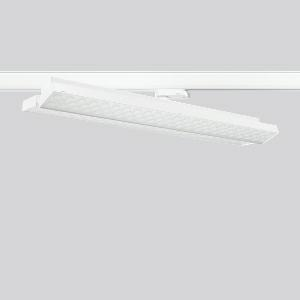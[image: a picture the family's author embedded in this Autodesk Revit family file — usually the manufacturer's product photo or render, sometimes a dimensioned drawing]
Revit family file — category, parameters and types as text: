
# Revit family: tx-move_742163_002_3_76_4216
name_source: partatom
category: Lighting Fixtures
units: mm (PartAtom-declared; Revit-internal decimal feet)

## family parameters
Cut with Voids When Loaded = No
Host = Face
Light Source = No
Part Type = Normal
Room Calculation Point = No
Round Connector Dimension = Use Diameter
Shared = No

## types (1)
- MultiLumen 1 (1 x LED Modul 835, 2875 lm, 3500)
    Apparent Load = 41 VA
    CIE Flux Codes = 65 90 98 100 100
    Color Rendering = 80
    Color Temperature = 3500
    Default Elevation = 1800 mm
    Description = Series: TX-MOVE
Multifunctional surface-mounted spotlight for area lighting. Very flat design. Housing: sheet steel, powder-coated. Rotation range: 356°. Swivel range: 90°. Consistent alignment possible with visible tilt scale. High-efficiency LED units with optimum light control thanks to clear plastic (PC) lens optics. Spezielle Mikrostrukturen reduzieren Gelbsaum. Asymmetrical light distribution. With adapter for RZB 3-circuit DALI tracks. Suitable for Track on ceiling. MultiLumen: Luminous flux adjustable in 3 steps. Factory setting is the highest luminous flux. Environmentally friendly and resource-saving due to replaceable and recyclable components. 
Colour: traffic white, matt (RAL 9016)
Length: 570 mm
Width: 119 mm
Height: 88 mm
Lamp: LED
Socket: without socket
Colour temperature: 3500K
Colour rendering index (CRI): 80
System power: 41 W
Rated luminous flux: 5750 lm
Luminous efficiency: 140 lm/W
System power 2: 57 W
Rated luminous flux 2: 7750 lm
Luminous efficiency 2: 136 lm/W
System power 3: 73 W
Rated luminous flux 3: 9450 lm
Luminous efficiency 3: 129 lm/W
Control gear: Dimmable EVG, DALI
Protection class: I
Type of protection: IP 20
    Height = 75 mm
    Lamp = 1 x LED Modul 835
    Lamp Light Flux = 2875 lm
    Lamp count = 1
    Length = 569 mm
    Lifetime = 50000 h
    Luminous efficacy = 140 lm/W
    Manufacturer = RZB
    ModVariant = No
    Model = 742163.002.3.76
    Mounting Place = Ceiling
    Mounting Type = Rail mounted
    Number of Poles = 1
    OnlyDefault = Yes
    Power Factor = 1
    Product Name = TX-MOVE
    Product group = Track mounted projectors
    ProductGroupID = 301
    Protection Class = Protection class I
    Protection Degree = IP 20
    RLX_Detail_Level = 1
    RLX_Emergency_Light_Flux = 0 lm
    RLX_Emergency_Type = 0
    RLX_Emergency_Type_DB = No
    RlxData = <blob elided: 51921 chars, md5=ae713f37>
    Socket = socket
    Standby Power = 0 W
    System Light Flux = 5750 lm
    System Power = 41 W
    Type Comments = MultiLumen 1
    Type Image = 742162.002.jpg
    URL = http://relux.com
    VarID = multilumen_1
    Voltage = 230 V
    Voltage Range = 220-240 V
    Weight = 0.00 kg
    Width = 119 mm

## geometry (parser evidence)
native form markers: Blend x4, Sweep x17
no freeform markers — native parametric forms only
